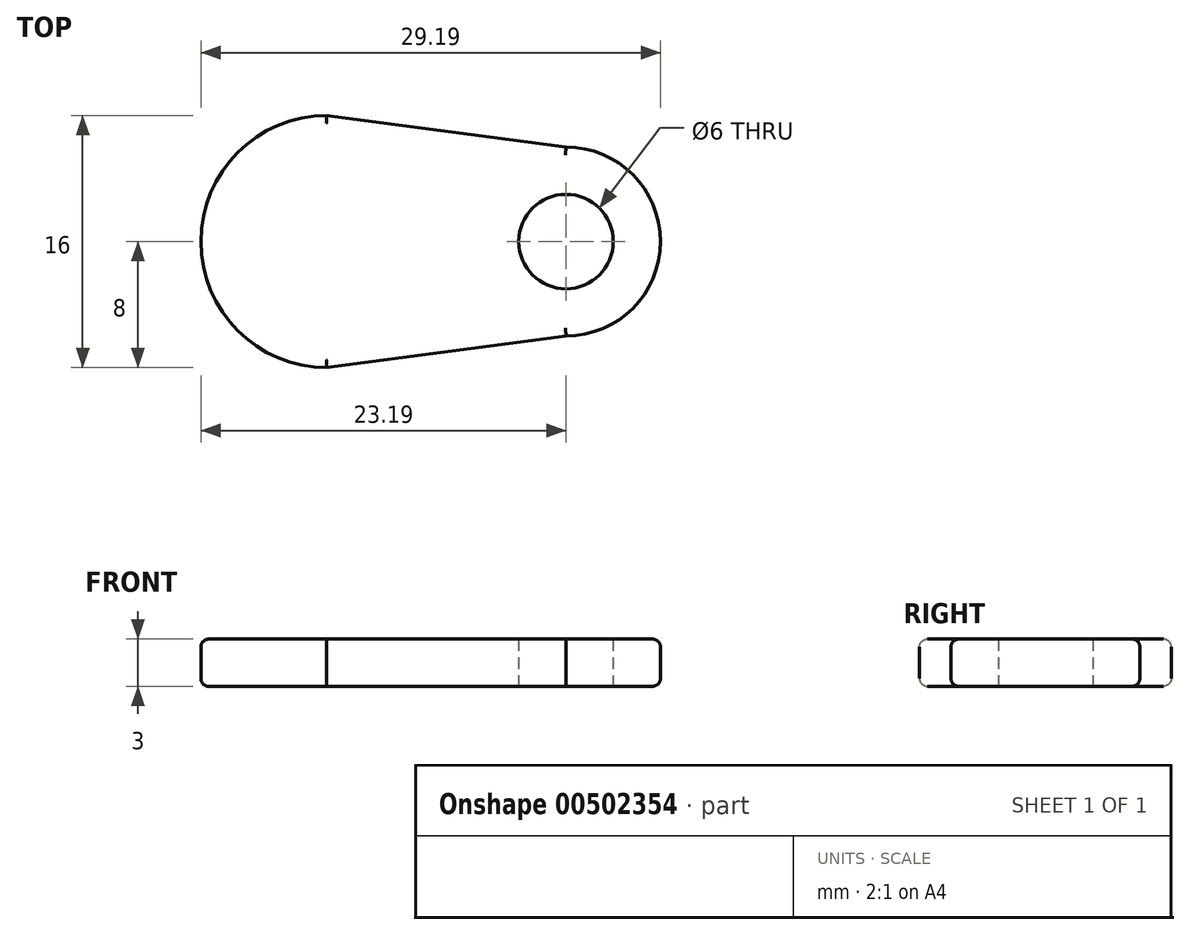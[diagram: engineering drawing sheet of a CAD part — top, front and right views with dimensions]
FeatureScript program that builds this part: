
annotation { "Feature Type Name" : "Feature", "Feature Type Description" : "" }
export const myFeature = defineFeature(function(context is Context, id is Id, definition is map)
    precondition{}
    {
        {
            var Q0;
            Q0=qCreatedBy(makeId("Top.planeOp"),FACE);
            var sketch = newSketch(context, id + "F0", { "sketchPlane" : qUnion([Q0])});
            skCircle(sketch, "E0", {"center": v(0, 0) * mm, "radius": 3 * mm});
            skArc(sketch, "E1", {"start": v(0, -6) * mm, "mid": v(6, 0) * mm, "end": v(0, 6) * mm});
            skLineSegment(sketch, "E2", {"start": v(0, 6) * mm, "end": v(-15.2, 8) * mm});
            skLineSegment(sketch, "E3.MirrorCS", {"start": v(0, -6) * mm, "end": v(-15.2, -8) * mm});
            skArc(sketch, "E4", {"start": v(-13.12, 7.73) * mm, "mid": v(-23.2, 0) * mm, "end": v(-13.12, -7.73) * mm});
            skSolve(sketch);
        }
        {
            var Q0;
            Q0=makeQuery(id+"F0.imprint","IMPRINT",FACE,{"disambiguationData":[TD([[makeQuery(id+"F0.imprint","IMPRINT",EDGE,{"derivedFrom":sQuery(id+"F0.wireOp",EDGE,"E0")}),-1.0]])]});
            extrude(context, id + "F1", {"entities" : qUnion([Q0]), "depth" : 3 * mm});
        }
        {
            var Q0;
            Q0=makeQuery(id+"F1.opExtrude","CAP_EDGE",EDGE,{"disambiguationData":[OSD([sQuery(id+"F0.wireOp",EDGE,"E4")])],"isStart":false});
            var Q1;
            Q1=makeQuery(id+"F1.opExtrude","CAP_EDGE",EDGE,{"disambiguationData":[OSD([sQuery(id+"F0.wireOp",EDGE,"E3.MirrorCS")])],"isStart":false});
            var Q2;
            Q2=makeQuery(id+"F1.opExtrude","CAP_EDGE",EDGE,{"disambiguationData":[OSD([sQuery(id+"F0.wireOp",EDGE,"E1")])],"isStart":false});
            var Q3;
            Q3=makeQuery(id+"F1.opExtrude","CAP_EDGE",EDGE,{"disambiguationData":[OSD([sQuery(id+"F0.wireOp",EDGE,"E2")])],"isStart":false});
            var Q4;
            Q4=makeQuery(id+"F1.opExtrude","CAP_EDGE",EDGE,{"disambiguationData":[OSD([sQuery(id+"F0.wireOp",EDGE,"E3.MirrorCS")])],"isStart":true});
            var Q5;
            Q5=makeQuery(id+"F1.opExtrude","CAP_EDGE",EDGE,{"disambiguationData":[OSD([sQuery(id+"F0.wireOp",EDGE,"E4")])],"isStart":true});
            var Q6;
            Q6=makeQuery(id+"F1.opExtrude","CAP_EDGE",EDGE,{"disambiguationData":[OSD([sQuery(id+"F0.wireOp",EDGE,"E1")])],"isStart":true});
            var Q7;
            Q7=makeQuery(id+"F1.opExtrude","CAP_EDGE",EDGE,{"disambiguationData":[OSD([sQuery(id+"F0.wireOp",EDGE,"E2")])],"isStart":true});
            fillet(context, id + "F2", {"entities" : qUnion([Q0, Q1, Q2, Q3, Q4, Q5, Q6, Q7]), "radius" : 0.5 * mm, "tangentPropagation" : true, "allowEdgeOverflow" : false});
        }
    });
